# Revit family: Double Hung without trim
name_source: partatom
category: Windows
revit_build: Autodesk Revit Architecture 2015 (Build: 20140322_1515(x64)
units: mm (PartAtom-declared; Revit-internal decimal feet)

## types (6) — shared parameters
Analytic Construction = <None>
Assembly Code = B2020100
Glass Pane Material = Glass
Sash Material = Sash
Trim Exterior Material = Trim
Trim Interior Material = Trim
Trim Projection - Ext. = 0' - 0 1/2"
Trim Projection - Int. = 0' - 0 3/4"
Trim Width - Exterior = 0' - 3 1/2"
Trim Width - Interior = 0' - 3 1/2"
Wall Closure = By host
Window Inset = 0' - 0 3/4"

## per-type parameters (varying)
| type | Default Sill Height | Height | Width |
| 13" x 23" | 1' - 0" | 1' - 11" | 1' - 1" |
| 23" x 23" | 3' - 0" | 1' - 11" | 1' - 11" |
| 24" x 36" | 3' - 0" | 3' - 0" | 2' - 0" |
| 24" x 48" | 1' - 0" | 4' - 0" | 2' - 0" |
| 30" x 48" | 1' - 0" | 4' - 0" | 2' - 6" |
| 36" x 48" | 1' - 0" | 4' - 0" | 3' - 0" |

## geometry (parser evidence)
native form markers: Sweep x1
no freeform markers — native parametric forms only
